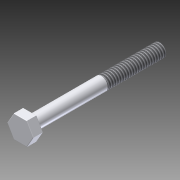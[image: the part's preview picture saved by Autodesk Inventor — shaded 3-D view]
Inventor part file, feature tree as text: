
AUTODESK INVENTOR PART (.ipt)
format: ipt  version: 2011 SP1 (Build 150282100, 282)  size: 100,352 bytes
history: native  units: in
note: dims shown in document units (in); Inventor stores cm internally (conversion verified against a paired STEP export)
features: extrude x2, sketch x2, fillet x1, thread x1
ambient origin geometry x8: Origin, YZ Plane, XZ Plane, XY Plane, X Axis, Y Axis, Z Axis, Center Point
bodies: Solid1 (feature_tree)
feature tree (6):
  extrude  "Extrusion1"  Depth=2.5in TaperAngle=0.0deg
  extrude  "Extrusion2"  Depth=0.1875in TaperAngle=0.0deg
  fillet  "Fillet1"  Radius=0.01in
  thread  "Thread1"  [1 undecoded]
  sketch  "Sketch1"  dims[d0=0.25in d1=2.5in d2=0.0in]
  sketch  "Sketch2"  dims[d4=0.4375in d5=0.1875in d6=0.0in d7=0.01in d8=1.125in d9=0.0in]
note: 1 required parameter value undecoded (feature->parameter linkage not recoverable at this tier; creation-order binding heuristic only, values carry confidence <= 0.55)
